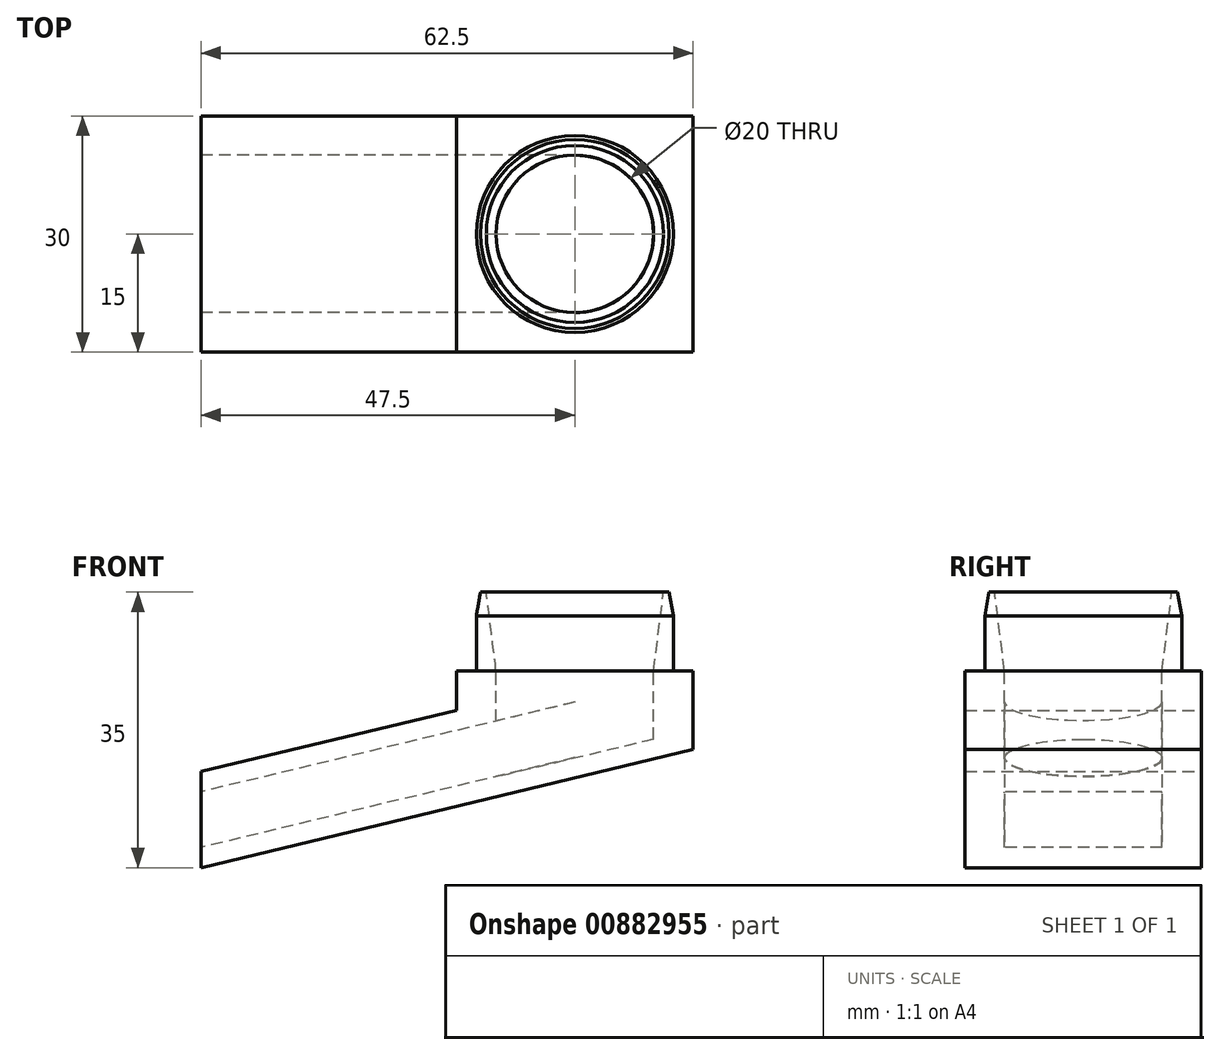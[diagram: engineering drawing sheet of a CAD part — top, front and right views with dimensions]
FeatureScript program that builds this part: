
annotation { "Feature Type Name" : "Feature", "Feature Type Description" : "" }
export const myFeature = defineFeature(function(context is Context, id is Id, definition is map)
    precondition{}
    {
        {
            var Q0;
            Q0=qCreatedBy(makeId("Front.planeOp"),FACE);
            var sketch = newSketch(context, id + "F0", { "sketchPlane" : qUnion([Q0])});
            skLineSegment(sketch, "E0", {"start": v(0, 0) * mm, "end": v(0, -14.65) * mm, "construction": true});
            skLineSegment(sketch, "E1", {"start": v(-15, 0) * mm, "end": v(-15, -5) * mm});
            skLineSegment(sketch, "E2", {"start": v(-15, -5) * mm, "end": v(-47.5, -12.8) * mm});
            skLineSegment(sketch, "E3", {"start": v(-47.5, -12.8) * mm, "end": v(-47.5, -25) * mm});
            skLineSegment(sketch, "E4", {"start": v(-47.5, -25) * mm, "end": v(15, -10) * mm});
            skLineSegment(sketch, "E5", {"start": v(15, -10) * mm, "end": v(15, 0) * mm});
            skLineSegment(sketch, "E6", {"start": v(15, 0) * mm, "end": v(-15, 0) * mm});
            skSolve(sketch);
        }
        {
            var Q0;
            Q0 = qSketchRegion(id + "F0", true);
            extrude(context, id + "F1", {"entities" : qUnion([Q0]), "endBound" : BoundingType.SYMMETRIC, "depth" : 30 * mm, "offsetDistance" : 25 * mm});
        }
        {
            var Q0;
            Q0=makeQuery(id+"F1.opExtrude","SWEPT_FACE",FACE,{"disambiguationData":[OSD([sQuery(id+"F0.wireOp",EDGE,"E6")])]});
            var sketch = newSketch(context, id + "F2", { "sketchPlane" : qUnion([Q0])});
            skCircle(sketch, "E7", {"center": v(0, 0) * mm, "radius": 10 * mm});
            skSolve(sketch);
        }
        {
            var Q0;
            Q0 = qSketchRegion(id + "F2", true);
            var Q1;
            Q1=makeQuery(id+"F1.opExtrude","SWEPT_FACE",FACE,{"disambiguationData":[OSD([sQuery(id+"F0.wireOp",EDGE,"E4")])]});
            extrude(context, id + "F3", {"entities" : qUnion([Q0]), "operationType" : NewBodyOperationType.REMOVE, "endBound" : BoundingType.UP_TO_SURFACE, "oppositeDirection" : true, "depth" : 25 * mm, "endBoundEntityFace" : qUnion([Q1]), "hasOffset" : true, "offsetDistance" : 2.5 * mm});
        }
        {
            var Q0;
            Q0=makeQuery(id+"F1.opExtrude","SWEPT_EDGE",EDGE,{"disambiguationData":[OSD([sQuery(id+"F0.wireOp",EDGE,"E3"),sQuery(id+"F0.wireOp",EDGE,"E4")])]});
            cPlane(context, id + "F4", {"entities" : qUnion([Q0]), "cplaneType" : CPlaneType.LINE_ANGLE, "offset" : 25 * mm, "angle" : 76.5 * degree, "width" : 150 * mm, "height" : 150 * mm});
        }
        {
            var Q0;
            Q0=qCreatedBy(id+"F4.planeOp",FACE);
            var sketch = newSketch(context, id + "F5", { "sketchPlane" : qUnion([Q0])});
            skLineSegment(sketch, "E8", {"start": v(15, -1.36) * mm, "end": v(-15, -13.22) * mm, "construction": true});
            skLineSegment(sketch, "E9", {"start": v(-15, -1.36) * mm, "end": v(15, -13.22) * mm, "construction": true});
            skLineSegment(sketch, "E10.bottom", {"start": v(-10, -3.86) * mm, "end": v(10, -3.86) * mm});
            skLineSegment(sketch, "E10.top", {"start": v(-10, -10.72) * mm, "end": v(10, -10.72) * mm});
            skLineSegment(sketch, "E10.left", {"start": v(-10, -3.86) * mm, "end": v(-10, -10.72) * mm});
            skLineSegment(sketch, "E10.right", {"start": v(10, -3.86) * mm, "end": v(10, -10.72) * mm});
            skPoint(sketch, "E10.middle", {"position": v(0, -7.3) * mm});
            skSolve(sketch);
        }
        {
            var Q0;
            Q0 = qSketchRegion(id + "F5", true);
            var Q1;
            Q1=makeQuery(id+"F3.boolean.opBoolean","COPY",FACE,{"derivedFrom":makeQuery(id+"F3.opExtrude","SWEPT_FACE",FACE,{"disambiguationData":[OSD([sQuery(id+"F2.wireOp",EDGE,"E7")])]})});
            extrude(context, id + "F6", {"entities" : qUnion([Q0]), "operationType" : NewBodyOperationType.REMOVE, "endBound" : BoundingType.UP_TO_SURFACE, "depth" : 25 * mm, "endBoundEntityFace" : qUnion([Q1]), "offsetDistance" : 25 * mm});
        }
        {
            var Q0;
            Q0=qCreatedBy(makeId("Front.planeOp"),FACE);
            var sketch = newSketch(context, id + "F7", { "sketchPlane" : qUnion([Q0])});
            skLineSegment(sketch, "E11", {"start": v(0, 0) * mm, "end": v(0, 13.45) * mm, "construction": true});
            skLineSegment(sketch, "E12", {"start": v(-10, 0) * mm, "end": v(-12.52, 0) * mm});
            skLineSegment(sketch, "E13", {"start": v(-12.52, 0) * mm, "end": v(-12.52, 7) * mm});
            skLineSegment(sketch, "E14", {"start": v(-12.52, 7) * mm, "end": v(-11.99, 10) * mm});
            skLineSegment(sketch, "E15", {"start": v(-11.99, 10) * mm, "end": v(-11.25, 10) * mm});
            skLineSegment(sketch, "E16", {"start": v(-11.25, 10) * mm, "end": v(-10, 0) * mm});
            skSolve(sketch);
        }
        {
            var Q0;
            Q0 = qSketchRegion(id + "F7", true);
            var Q1;
            Q1=sQuery(id+"F7.wireOp",EDGE,"E11");
            revolve(context, id + "F8", {"operationType" : NewBodyOperationType.ADD, "surfaceOperationType" : NewSurfaceOperationType.NEW, "entities" : qUnion([Q0]), "axis" : qUnion([Q1]), "revolveType" : RevolveType.FULL});
        }
    });
